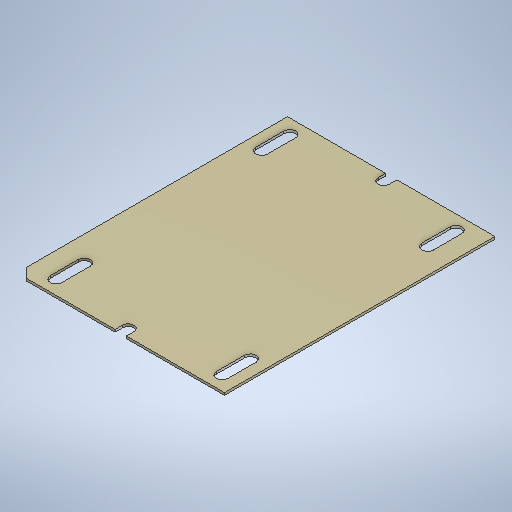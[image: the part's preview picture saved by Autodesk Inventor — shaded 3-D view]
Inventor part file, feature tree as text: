
AUTODESK INVENTOR PART (.ipt)
format: ipt  version: 2025 (Build 290162000, 162)  size: 381,952 bytes
history: native  units: in
note: dims shown in document units (in); Inventor stores cm internally (conversion verified against a paired STEP export)
features: extrude x5, sketch x3, hole x1
ambient origin geometry x8: Origin, YZ Plane, XZ Plane, XY Plane, X Axis, Y Axis, Z Axis, Center Point
bodies: Body1 (feature_tree)
feature tree (9):
  extrude  "Extrusion2"  Depth=2.2638in
  extrude  "Extrusion3"  Depth=0.0984in
  hole  "Hole1"  [1 undecoded]
  extrude  "Extrusion4"  TaperAngle=0.0deg  [1 undecoded]
  extrude  "Extrusion5"  Depth=0.0492in
  extrude  "Extrusion6"  Depth=0.0492in
  sketch  "Sketch3"  dims[d28=1.7362in d29=2.2638in]
  sketch  "Sketch6"  dims[d30=0.0197in d31=0.0in d32=0.0984in]
  sketch  "Sketch7"  dims[d33=0.3543in d34=0.0492in d35=0.0in d36=0.0in d37=0.8681in d38=0.063in d40=0.063in d41=0.0945in d42=0.1575in d43=0.1732in d44=0.0787in d45=0.6181in d46=0.315in d47=0.8108in d48=0.2087in d49=0.0787in d50=0.0787in d51=0.0in d52=0.0in d60=0.3543in d61=0.3543in d62=0.0492in d64=0.3543in d65=0.3543in d66=0.0492in d68=1.7362in d69=0.3937in d70=0.0in d71=0.1378in d73=0.0492in d74=0.0492in d75=0.1181in d76=0.3937in d77=0.0in d78=0.0492in d79=0.0492in d80=0.1181in d81=0.0492in d82=0.1181in d85=0.0492in d86=0.1181in d87=0.2087in d88=0.1378in]
note: 2 required parameter values undecoded (feature->parameter linkage not recoverable at this tier; creation-order binding heuristic only, values carry confidence <= 0.55)
